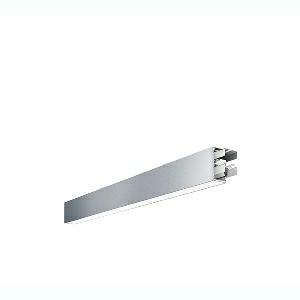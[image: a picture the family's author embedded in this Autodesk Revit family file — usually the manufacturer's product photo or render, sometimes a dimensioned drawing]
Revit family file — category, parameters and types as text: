
# Revit family: dotoo_line_-_dla_1000_830_d_sta_00807961_bb8a
name_source: partatom
category: Lighting Fixtures
units: mm (PartAtom-declared; Revit-internal decimal feet)

## family parameters
Cut with Voids When Loaded = No
Host = Face
Light Source = No
Part Type = Normal
Room Calculation Point = No
Round Connector Dimension = Use Diameter
Shared = No

## types (1)
- DOTOO.line - DLA 1000/830/D STA (1 x LED, 1000 lm, 3000K)
    Apparent Load = 10 VA
    Approval mark = CE
    CIE Flux Codes = 67 91 98 100 100
    Color Rendering = 80-89
    Color Temperature = 3000K
    Control Gear = Electronic ballast
    Default Elevation = 1800 mm
    Description = DLA 1000/830/D|Surface-mounted luminaire.|light source: LED|work equipment: Adjustable electronic ballast, digital DALI|connected load: 220-240 V, 50/60 Hz|Power consumption: approx. 10 W|luminous flux: 1000 lm|luminous efficacy: 100 lm/W|light distribution: Direct|colour temperature: Warm white, ca. 3000 K|class of protection: I|technology: Continuously dimmable|mains lead: Connector|glare control: Prism aperture|special features: DALI Load 1x, TouchDIM - dimming via standard switch, Through-wired, up to 18 m on one mains connection, Flicker-free, Suitable as emergency lighting, Start luminaire with mains connection, Maintenance-friendly due to easily accessible ballasts|
    Frequency = 50 Hz
    Height = 110 mm
    Lamp = 1 x LED
    Lamp Light Flux = 1000 lm
    Lamp count = 1
    Length = 848 mm
    Luminous efficacy = 100 lm/W
    Manufacturer = Waldmann
    ModVariant = No
    Model = 00807961
    Mounting Place = Ceiling
    Mounting Type = Surface mounted
    Number of Poles = 1
    OnlyDefault = Yes
    Power Factor = 1
    Product Name = DOTOO.line - DLA 1000/830/D STA
    Product group = Ceiling mounted luminaire
    ProductGroupID = 3
    Protection Class = Protection class I
    Protection Degree = IP 40
    RLX_Detail_Level = 1
    RLX_Emergency_Light_Flux = 0 lm
    RLX_Emergency_Type = 0
    RLX_Emergency_Type_DB = No
    RlxData = <blob elided: 18317 chars, md5=e99ab093>
    Socket = socket
    Standby Power = 0 W
    System Light Flux = 1000 lm
    System Power = 10 W
    Type Comments = Product without accessories
    Type Image = 114372000-00807949.jpg
    URL = http://relux.com
    VarID = ---
    Voltage = 230 V
    Voltage Range = 220-240 V
    Weight = 0.00 kg
    Width = 60 mm  [stored 0.19685 ft]

note: [stored X ft] marks values corroborated as IEEE doubles in the binary element streams (Revit-internal decimal feet)

## geometry (parser evidence)
native form markers: Blend x4, Sweep x11
no freeform markers — native parametric forms only
